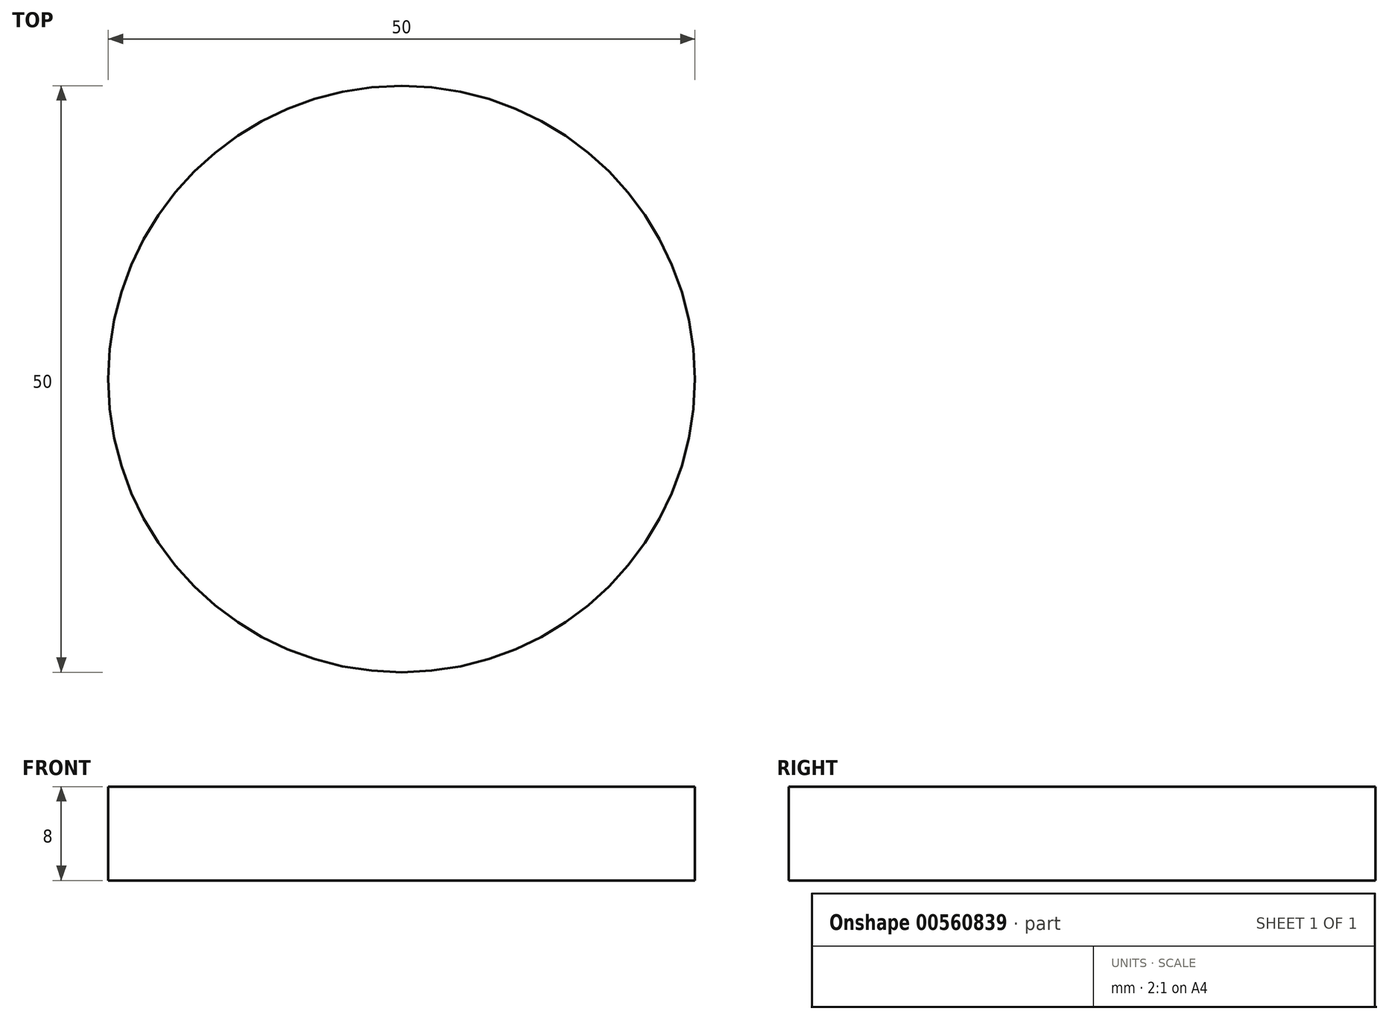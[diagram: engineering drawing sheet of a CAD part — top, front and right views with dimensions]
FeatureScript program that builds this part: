
annotation { "Feature Type Name" : "Feature", "Feature Type Description" : "" }
export const myFeature = defineFeature(function(context is Context, id is Id, definition is map)
    precondition{}
    {
        {
            var Q0;
            Q0=qCreatedBy(makeId("Top.planeOp"),FACE);
            var sketch = newSketch(context, id + "F0", { "sketchPlane" : qUnion([Q0])});
            skCircle(sketch, "E0", {"center": v(0, 0) * mm, "radius": 25 * mm});
            skSolve(sketch);
        }
        {
            var Q0;
            Q0=makeQuery(id+"F0.imprint","IMPRINT",FACE,{"disambiguationData":[TD([[makeQuery(id+"F0.imprint","IMPRINT",EDGE,{"derivedFrom":sQuery(id+"F0.wireOp",EDGE,"E0")}),1.0]])]});
            extrude(context, id + "F1", {"entities" : qUnion([Q0]), "depth" : 8 * mm, "offsetDistance" : 25.4 * mm});
        }
    });
